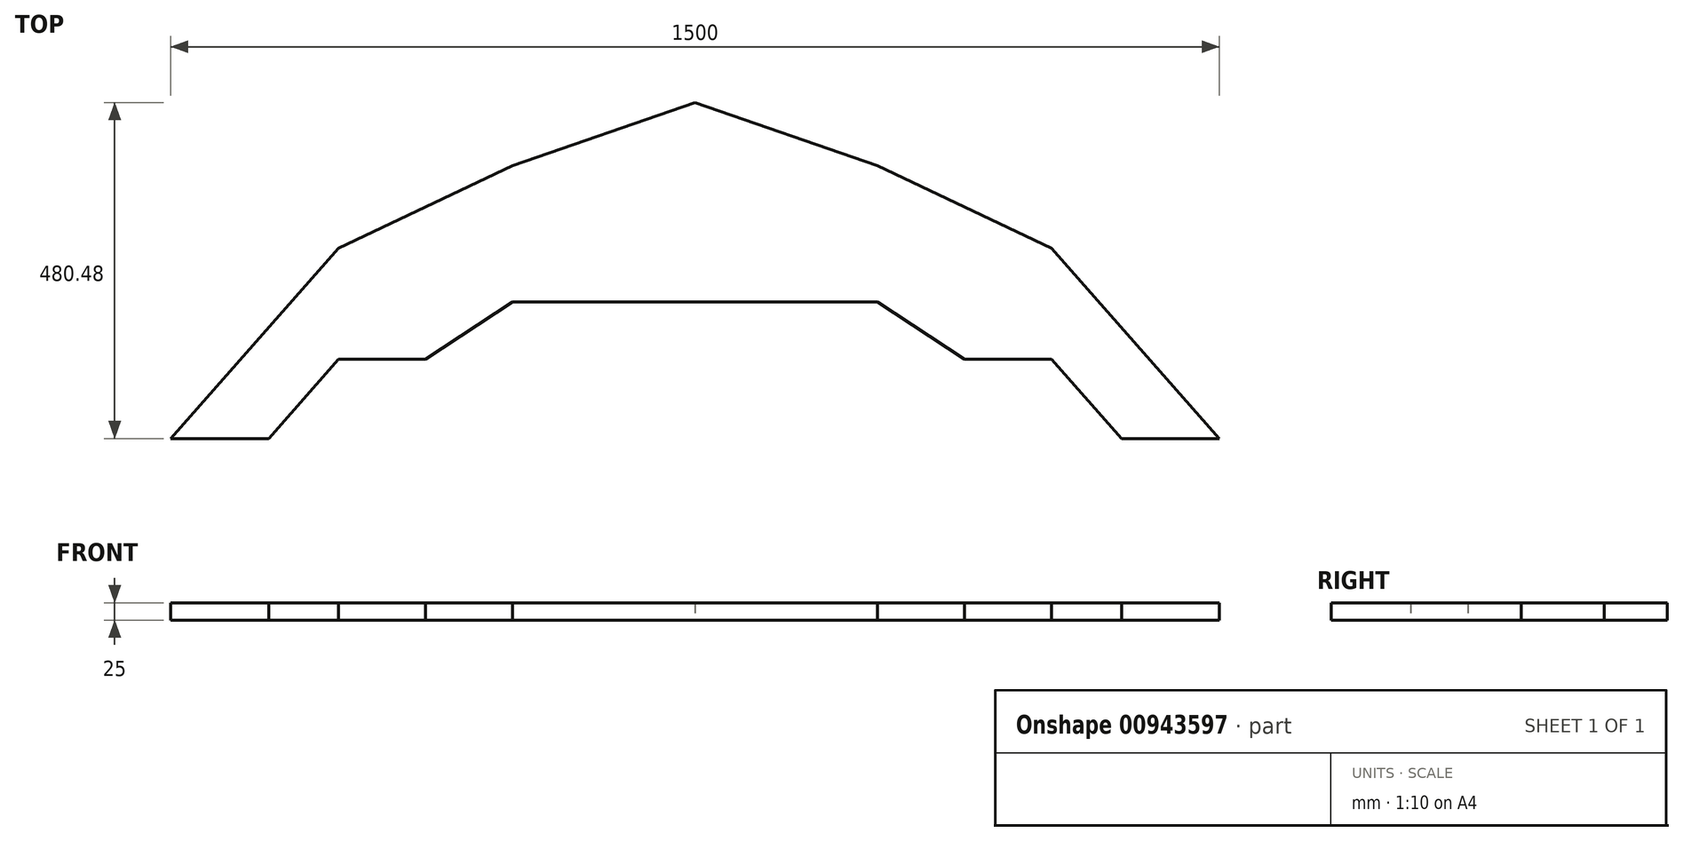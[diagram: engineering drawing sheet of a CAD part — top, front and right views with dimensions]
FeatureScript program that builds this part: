
annotation { "Feature Type Name" : "Feature", "Feature Type Description" : "" }
export const myFeature = defineFeature(function(context is Context, id is Id, definition is map)
    precondition{}
    {
        {
            var Q0;
            Q0=qCreatedBy(makeId("Top.planeOp"),FACE);
            var sketch = newSketch(context, id + "F0", { "sketchPlane" : qUnion([Q0])});
            skLineSegment(sketch, "E0", {"start": v(-750, 0) * mm, "end": v(0, 0) * mm});
            skLineSegment(sketch, "E1", {"start": v(750, 0) * mm, "end": v(0, 0) * mm});
            skLineSegment(sketch, "E2", {"start": v(-261, 390.48) * mm, "end": v(0, 390.48) * mm});
            skLineSegment(sketch, "E3", {"start": v(0, 390.48) * mm, "end": v(261, 390.48) * mm});
            skLineSegment(sketch, "E4", {"start": v(0, 0) * mm, "end": v(0, 390.48) * mm});
            skLineSegment(sketch, "E5", {"start": v(0, 480.48) * mm, "end": v(0, 390.48) * mm});
            skLineSegment(sketch, "E6", {"start": v(-261, 390.48) * mm, "end": v(0, 480.48) * mm});
            skLineSegment(sketch, "E7", {"start": v(0, 480.48) * mm, "end": v(261, 390.48) * mm});
            skLineSegment(sketch, "E8", {"start": v(0, 0) * mm, "end": v(0, 271.9) * mm});
            skLineSegment(sketch, "E9", {"start": v(0, 271.9) * mm, "end": v(-510, 271.9) * mm});
            skLineSegment(sketch, "E10", {"start": v(0, 271.9) * mm, "end": v(510, 271.9) * mm});
            skLineSegment(sketch, "E11", {"start": v(-261, 390.48) * mm, "end": v(-510, 271.9) * mm});
            skLineSegment(sketch, "E12", {"start": v(-510, 271.9) * mm, "end": v(-750, 0) * mm});
            skLineSegment(sketch, "E13", {"start": v(261, 390.48) * mm, "end": v(510, 271.9) * mm});
            skLineSegment(sketch, "E14", {"start": v(510, 271.9) * mm, "end": v(750, 0) * mm});
            skSolve(sketch);
        }
        {
            var Q0;
            Q0=makeQuery(id+"F0.imprint","IMPRINT",FACE,{"disambiguationData":[TD([[makeQuery(id+"F0.imprint","IMPRINT",EDGE,{"derivedFrom":sQuery(id+"F0.wireOp",EDGE,"E0")}),1.0]])]});
            var Q1;
            Q1=makeQuery(id+"F0.imprint","IMPRINT",FACE,{"disambiguationData":[TD([[makeQuery(id+"F0.imprint","IMPRINT",EDGE,{"derivedFrom":sQuery(id+"F0.wireOp",EDGE,"E2")}),-1.0]])]});
            var Q2;
            Q2=makeQuery(id+"F0.imprint","IMPRINT",FACE,{"disambiguationData":[TD([[makeQuery(id+"F0.imprint","IMPRINT",EDGE,{"derivedFrom":sQuery(id+"F0.wireOp",EDGE,"E2")}),1.0]])]});
            var Q3;
            Q3=makeQuery(id+"F0.imprint","IMPRINT",FACE,{"disambiguationData":[TD([[makeQuery(id+"F0.imprint","IMPRINT",EDGE,{"derivedFrom":sQuery(id+"F0.wireOp",EDGE,"E3")}),1.0]])]});
            var Q4;
            Q4=makeQuery(id+"F0.imprint","IMPRINT",FACE,{"disambiguationData":[TD([[makeQuery(id+"F0.imprint","IMPRINT",EDGE,{"derivedFrom":sQuery(id+"F0.wireOp",EDGE,"E3")}),-1.0]])]});
            var Q5;
            Q5=makeQuery(id+"F0.imprint","IMPRINT",FACE,{"disambiguationData":[TD([[makeQuery(id+"F0.imprint","IMPRINT",EDGE,{"derivedFrom":sQuery(id+"F0.wireOp",EDGE,"E1")}),-1.0]])]});
            extrude(context, id + "F1", {"entities" : qUnion([Q0, Q1, Q2, Q3, Q4, Q5]), "depth" : 25 * mm, "offsetDistance" : 25 * mm});
        }
        {
            var Q0;
            Q0=makeQuery(id+"F1.opExtrude","CAP_FACE",FACE,{"disambiguationData":[OSD([sQuery(id+"F0.wireOp",EDGE,"E0"),sQuery(id+"F0.wireOp",EDGE,"E1"),sQuery(id+"F0.wireOp",EDGE,"E6"),sQuery(id+"F0.wireOp",EDGE,"E7"),sQuery(id+"F0.wireOp",EDGE,"E11"),sQuery(id+"F0.wireOp",EDGE,"E12"),sQuery(id+"F0.wireOp",EDGE,"E13"),sQuery(id+"F0.wireOp",EDGE,"E14")])],"isStart":true});
            var sketch = newSketch(context, id + "F2", { "sketchPlane" : qUnion([Q0])});
            skLineSegment(sketch, "E15", {"start": v(-750, 0) * mm, "end": v(-610, 0) * mm});
            skLineSegment(sketch, "E16", {"start": v(-610, 0) * mm, "end": v(-510, -113.29) * mm});
            skLineSegment(sketch, "E17", {"start": v(750, 0) * mm, "end": v(610, 0) * mm});
            skLineSegment(sketch, "E18", {"start": v(610, 0) * mm, "end": v(510, -113.29) * mm});
            skLineSegment(sketch, "E19", {"start": v(385.5, -113.29) * mm, "end": v(261, -195.24) * mm});
            skLineSegment(sketch, "E20", {"start": v(261, -195.24) * mm, "end": v(-261, -195.24) * mm});
            skLineSegment(sketch, "E21", {"start": v(-261, -195.24) * mm, "end": v(-385.5, -113.29) * mm});
            skLineSegment(sketch, "E22", {"start": v(385.5, -113.29) * mm, "end": v(510, -113.29) * mm});
            skLineSegment(sketch, "E23", {"start": v(-385.5, -113.29) * mm, "end": v(-510, -113.29) * mm});
            skSolve(sketch);
        }
        {
            var Q0;
            {var subQ1=sQuery(id+"F2.wireOp",EDGE,"E16");Q0=makeQuery(id+"F2.imprint","IMPRINT",FACE,{"disambiguationData":[TD([[makeQuery(id+"F2.imprint","IMPRINT",EDGE,{"derivedFrom":subQ1}),1.0]])]});}
            extrude(context, id + "F3", {"entities" : qUnion([Q0]), "operationType" : NewBodyOperationType.REMOVE, "oppositeDirection" : true, "depth" : 25 * mm, "offsetDistance" : 25 * mm});
        }
        {
            var Q0;
            Q0=makeQuery(id+"F1.opExtrude","CAP_FACE",FACE,{"disambiguationData":[OSD([sQuery(id+"F0.wireOp",EDGE,"E0"),sQuery(id+"F0.wireOp",EDGE,"E1"),sQuery(id+"F0.wireOp",EDGE,"E6"),sQuery(id+"F0.wireOp",EDGE,"E7"),sQuery(id+"F0.wireOp",EDGE,"E11"),sQuery(id+"F0.wireOp",EDGE,"E12"),sQuery(id+"F0.wireOp",EDGE,"E13"),sQuery(id+"F0.wireOp",EDGE,"E14")])],"isStart":false});
            var sketch = newSketch(context, id + "F4", { "sketchPlane" : qUnion([Q0])});
            skLineSegment(sketch, "E24", {"start": v(100, 195.24) * mm, "end": v(100, 95.24) * mm});
            skLineSegment(sketch, "E25", {"start": v(-100, 195.24) * mm, "end": v(-100, 95.24) * mm});
            skLineSegment(sketch, "E26", {"start": v(-100, 95.24) * mm, "end": v(100, 95.24) * mm});
            skLineSegment(sketch, "E27", {"start": v(100, 95.24) * mm, "end": v(100, 195.24) * mm});
            skSolve(sketch);
        }
        {
            var Q0;
            {var subQ0=sQuery(id+"F4.wireOp",EDGE,"E25");Q0=makeQuery(id+"F4.imprint","IMPRINT",FACE,{"disambiguationData":[TD([[makeQuery(id+"F4.imprint","IMPRINT",EDGE,{"derivedFrom":subQ0}),1.0]])]});}
            extrude(context, id + "F5", {"entities" : qUnion([Q0]), "oppositeDirection" : true, "depth" : 25 * mm, "offsetDistance" : 25 * mm});
        }
        {
            var Q0;
            Q0=makeQuery(id+"F5.opExtrude","SWEPT_BODY",BODY,{"disambiguationData":[OSD([sQuery(id+"F2.wireOp",EDGE,"E20"),sQuery(id+"F4.wireOp",EDGE,"E25"),sQuery(id+"F4.wireOp",EDGE,"E26"),sQuery(id+"F4.wireOp",EDGE,"E27")])]});
            deleteBodies(context, id + "F6", {"entities" : qUnion([Q0])});
        }
    });
